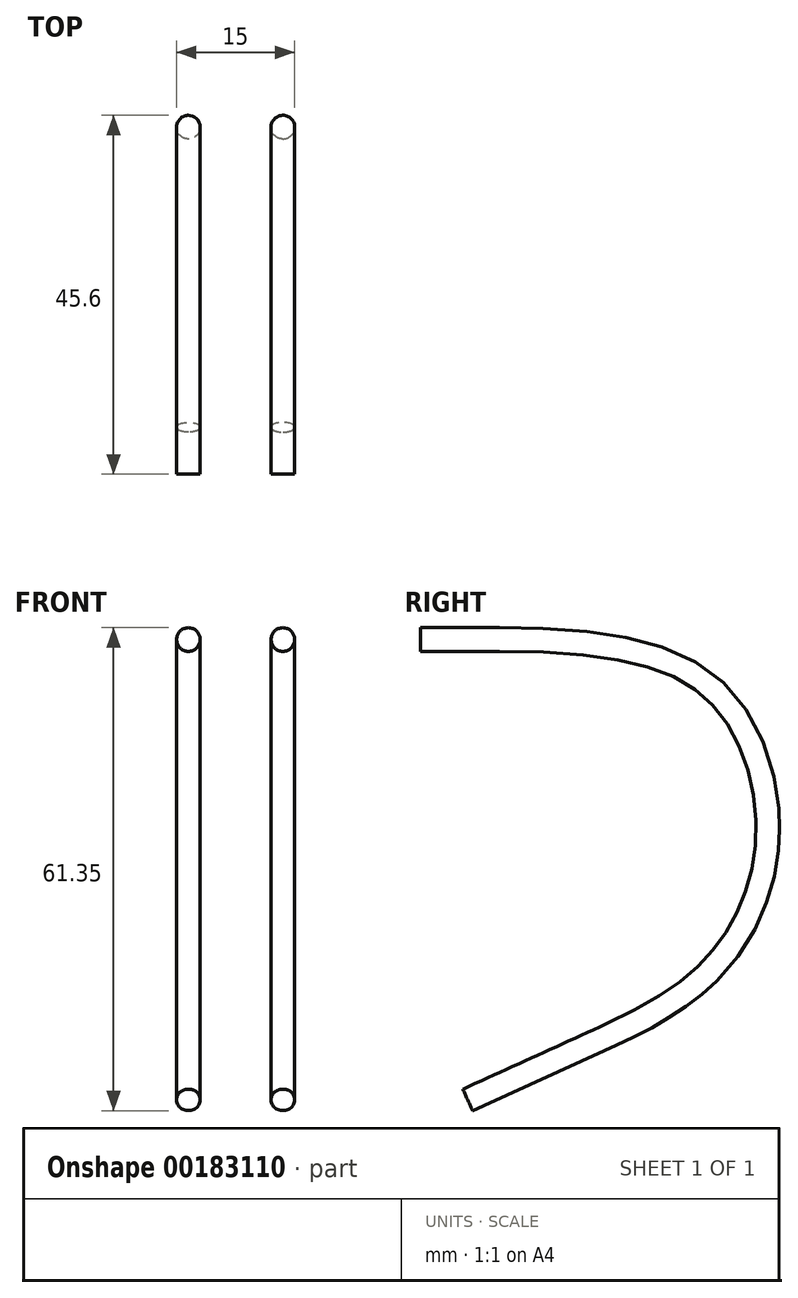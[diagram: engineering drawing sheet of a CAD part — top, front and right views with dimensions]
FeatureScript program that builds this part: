
annotation { "Feature Type Name" : "Feature", "Feature Type Description" : "" }
export const myFeature = defineFeature(function(context is Context, id is Id, definition is map)
    precondition{}
    {
        {
            var Q0;
            Q0=qCreatedBy(makeId("Right.planeOp"),FACE);
            cPlane(context, id + "F0", {"entities" : qUnion([Q0]), "cplaneType" : CPlaneType.OFFSET, "offset" : 6 * mm, "width" : 150 * mm, "height" : 150 * mm});
        }
        {
            var Q0;
            Q0=qCreatedBy(id+"F0.planeOp",FACE);
            var sketch = newSketch(context, id + "F1", { "sketchPlane" : qUnion([Q0])});
            skLineSegment(sketch, "E0", {"start": v(0, 0) * mm, "end": v(18.2, 8.27) * mm});
            skLineSegment(sketch, "E1", {"start": v(-5.97, 58.48) * mm, "end": v(4.03, 58.48) * mm});
            skFitSpline(sketch, "E2", {"points": [v(4.03, 58.48) * mm, v(31.94, 51.48) * mm, v(38.13, 34.32) * mm, v(33.34, 19.41) * mm, v(18.2, 8.27) * mm], "startDerivative": vector(138.06, 0) * mm, "endDerivative": vector(-90.84, -41.28) * mm});
            skSolve(sketch);
        }
        {
            var Q0;
            Q0=sQuery(id+"F1.wireOp",VERTEX,"E0.start");
            var Q1;
            Q1=sQuery(id+"F1.wireOp",EDGE,"E0");
            cPlane(context, id + "F2", {"entities" : qUnion([Q0, Q1]), "cplaneType" : CPlaneType.LINE_POINT, "offset" : 25 * mm, "width" : 150 * mm, "height" : 150 * mm});
        }
        {
            var Q0;
            Q0=qCreatedBy(id+"F2.planeOp",FACE);
            var sketch = newSketch(context, id + "F3", { "sketchPlane" : qUnion([Q0])});
            skCircle(sketch, "E3", {"center": v(-6, 0) * mm, "radius": 1.5 * mm});
            skSolve(sketch);
        }
        {
            var Q0;
            Q0 = qSketchRegion(id + "F3", true);
            var Q1;
            Q1 = qConstructionFilter(qBodyType(qCreatedBy(id + "F1" ,EDGE), BodyType.WIRE), ConstructionObject.NO);
            sweep(context, id + "F4", {"profiles" : qUnion([Q0]), "path" : qUnion([Q1])});
        }
        {
            var Q0;
            Q0=makeQuery(id+"F4.opSweep","SWEPT_BODY",BODY,{"disambiguationData":[OSD([sQuery(id+"F1.wireOp",EDGE,"E0"),sQuery(id+"F3.wireOp",EDGE,"E3")])]});
            var Q1;
            Q1=qCreatedBy(makeId("Right.planeOp"),FACE);
            mirror(context, id + "F5", {"entities" : qUnion([Q0]), "mirrorPlane" : qUnion([Q1])});
        }
    });
